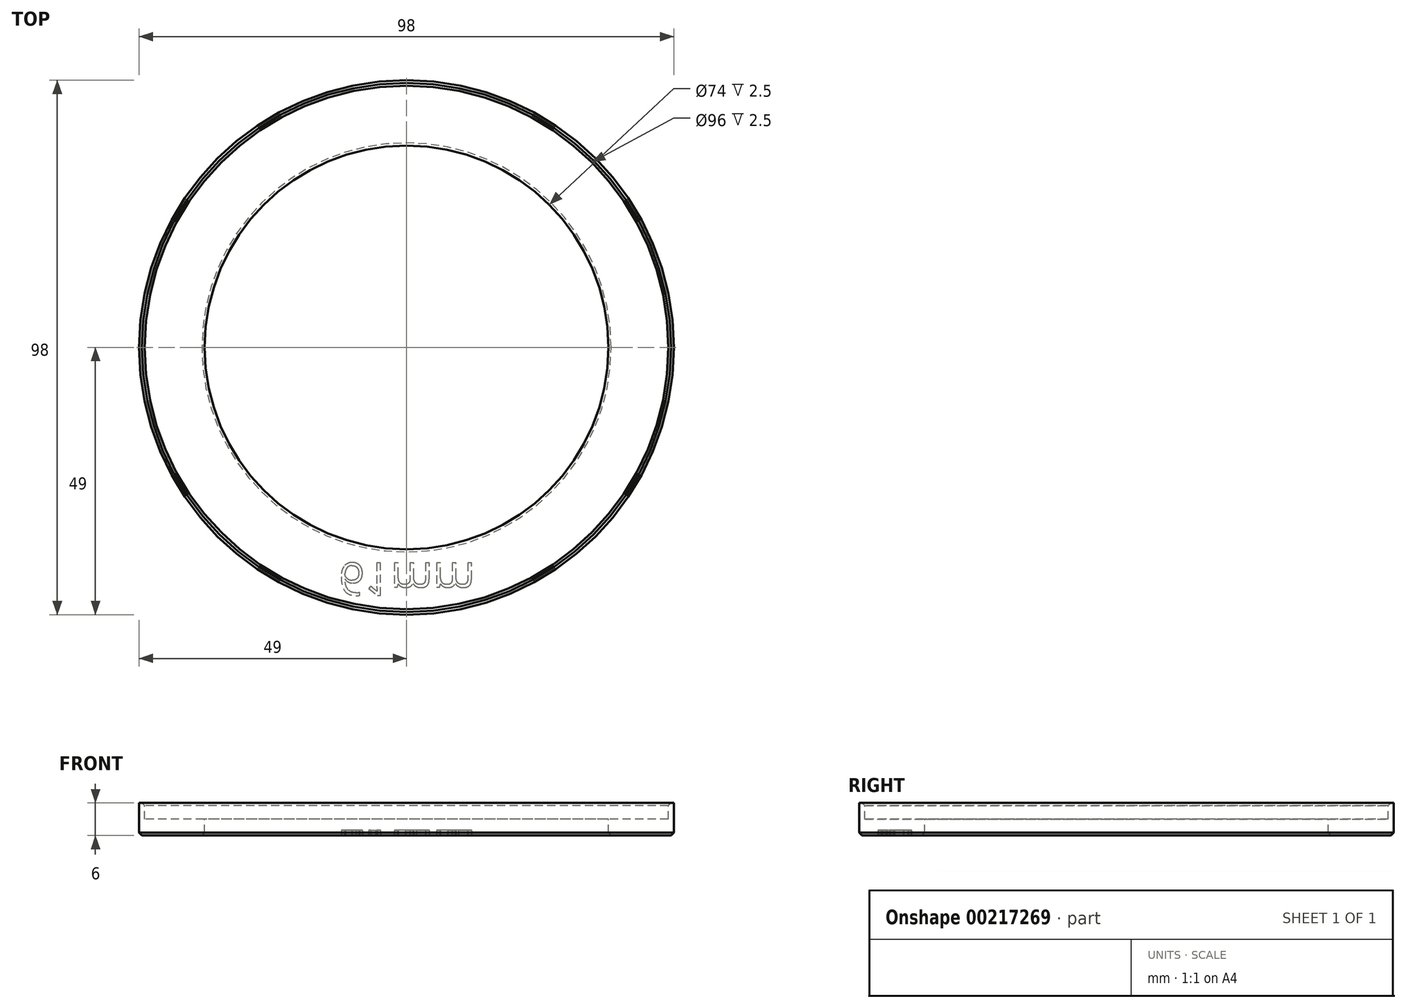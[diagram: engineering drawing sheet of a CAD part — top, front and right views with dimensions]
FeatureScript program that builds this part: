
annotation { "Feature Type Name" : "Feature", "Feature Type Description" : "" }
export const myFeature = defineFeature(function(context is Context, id is Id, definition is map)
    precondition{}
    {
        {
            var Q0;
            Q0=qCreatedBy(makeId("Front.planeOp"),FACE);
            var sketch = newSketch(context, id + "F0", { "sketchPlane" : qUnion([Q0])});
            skLineSegment(sketch, "E0", {"start": v(-49, 6) * mm, "end": v(-49, 0) * mm});
            skLineSegment(sketch, "E1", {"start": v(-49, 0) * mm, "end": v(-37, 0) * mm});
            skLineSegment(sketch, "E2", {"start": v(-37, 0) * mm, "end": v(-37, 3) * mm});
            skLineSegment(sketch, "E3", {"start": v(-37, 3) * mm, "end": v(-48, 3) * mm});
            skLineSegment(sketch, "E4", {"start": v(-48, 3) * mm, "end": v(-48, 6) * mm});
            skLineSegment(sketch, "E5", {"start": v(-48, 6) * mm, "end": v(-49, 6) * mm});
            skLineSegment(sketch, "E6", {"start": v(0, 62.77) * mm, "end": v(0, -27.64) * mm, "construction": true});
            skSolve(sketch);
        }
        {
            var Q0;
            Q0 = qSketchRegion(id + "F0", true);
            var Q1;
            Q1 = qSketchRegion(id + "F3", true);
            var Q2;
            Q2=sQuery(id+"F0.wireOp",EDGE,"E6");
            revolve(context, id + "F1", {"surfaceOperationType" : NewSurfaceOperationType.NEW, "entities" : qUnion([Q0, Q1]), "axis" : qUnion([Q2]), "revolveType" : RevolveType.FULL});
        }
        {
            var Q0;
            Q0=makeQuery(id+"F1.opRevolve","SWEPT_FACE",FACE,{"disambiguationData":[OSD([sQuery(id+"F0.wireOp",EDGE,"E1")])]});
            var Q1;
            Q1=makeQuery(id+"F1.opRevolve","SWEPT_EDGE",EDGE,{"disambiguationData":[OSD([sQuery(id+"F0.wireOp",EDGE,"E4"),sQuery(id+"F0.wireOp",EDGE,"E5")])]});
            chamfer(context, id + "F2", {"entities" : qUnion([Q0, Q1]), "width" : .5 * mm, "tangentPropagation" : true});
        }
        {
            var Q0;
            Q0=makeQuery(id+"F1.opRevolve","SWEPT_FACE",FACE,{"disambiguationData":[OSD([sQuery(id+"F0.wireOp",EDGE,"E1")])]});
            var sketch = newSketch(context, id + "F3", { "sketchPlane" : qUnion([Q0])});
            skText(sketch, "E7", { "text": "61mm", "fontName": "OpenSans-Regular.ttf"});
            skCircle(sketch, "E8", {"center": v(0, 0) * mm, "radius": 39.5 * mm, "construction": true});
            const initialGuessF3  = {"E7": [-0.01245, 0.0395, 1, 0, 0.006]};
            skSetInitialGuess(sketch, initialGuessF3);
            skSolve(sketch);
        }
        {
            var Q0;
            Q0 = qSketchRegion(id + "F3", true);
            var Q1;
            Q1=makeQuery(id+"F1.opRevolve","SWEPT_FACE",FACE,{"disambiguationData":[OSD([sQuery(id+"F0.wireOp",EDGE,"E5")])]});
            extrude(context, id + "F4", {"entities" : qUnion([Q0, Q1]), "operationType" : NewBodyOperationType.REMOVE, "oppositeDirection" : true, "depth" : 1 * mm, "offsetDistance" : 25 * mm});
        }
    });
